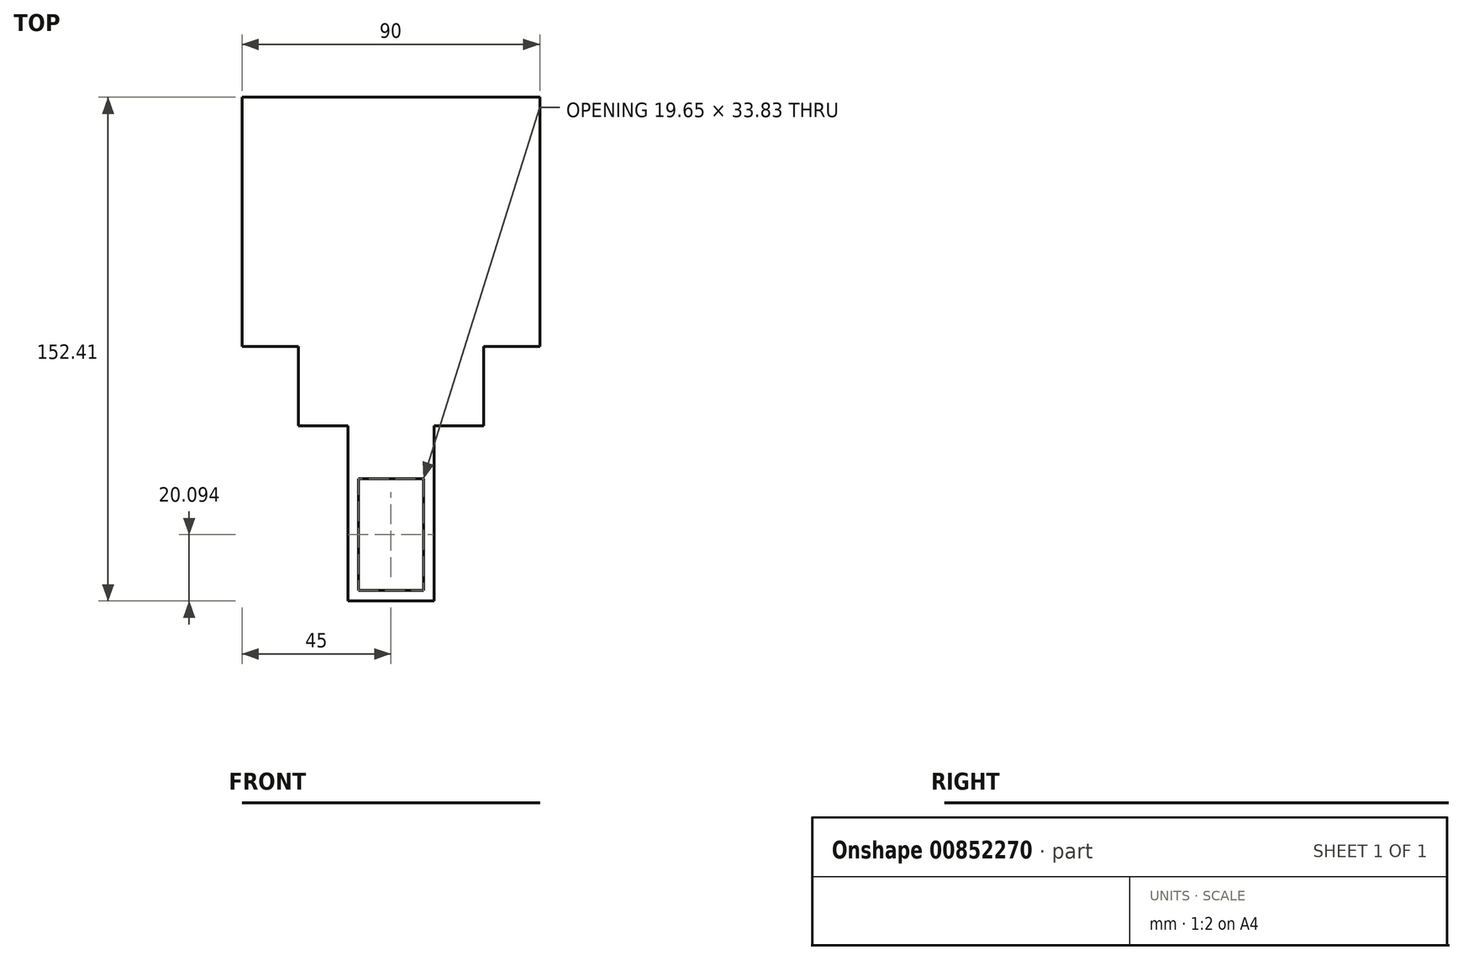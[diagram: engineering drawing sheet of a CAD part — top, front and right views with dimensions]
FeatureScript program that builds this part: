
annotation { "Feature Type Name" : "Feature", "Feature Type Description" : "" }
export const myFeature = defineFeature(function(context is Context, id is Id, definition is map)
    precondition{}
    {
        {
            var Q0;
            Q0=qCreatedBy(makeId("Top.planeOp"),FACE);
            var sketch = newSketch(context, id + "F0", { "sketchPlane" : qUnion([Q0])});
            skLineSegment(sketch, "E0.bottom", {"start": v(0, 0) * mm, "end": v(56, 0) * mm});
            skLineSegment(sketch, "E0.top", {"start": v(0, -74) * mm, "end": v(56, -74) * mm});
            skLineSegment(sketch, "E0.left", {"start": v(0, 0) * mm, "end": v(0, -74) * mm});
            skLineSegment(sketch, "E0.right", {"start": v(56, 0) * mm, "end": v(56, -74) * mm});
            skPoint(sketch, "E1", {"position": v(28, -74) * mm});
            skLineSegment(sketch, "E2", {"start": v(28, -74) * mm, "end": v(15, -74) * mm});
            skLineSegment(sketch, "E3", {"start": v(28, -74) * mm, "end": v(41, -74) * mm});
            skLineSegment(sketch, "E4", {"start": v(41, -74) * mm, "end": v(41, -90) * mm});
            skLineSegment(sketch, "E5", {"start": v(41, -90) * mm, "end": v(15, -90) * mm});
            skLineSegment(sketch, "E6", {"start": v(15, -74) * mm, "end": v(15, -90) * mm});
            skLineSegment(sketch, "E7", {"start": v(56, 0) * mm, "end": v(56, -23) * mm});
            skLineSegment(sketch, "E8", {"start": v(0, 0) * mm, "end": v(0, -23) * mm});
            skLineSegment(sketch, "E9", {"start": v(56, 0) * mm, "end": v(73, 0) * mm});
            skLineSegment(sketch, "E10", {"start": v(0, 0) * mm, "end": v(-17, 0) * mm});
            skPoint(sketch, "E11", {"position": v(28, 0) * mm});
            skPoint(sketch, "E12", {"position": v(28, -90) * mm});
            skLineSegment(sketch, "E13", {"start": v(28, -90) * mm, "end": v(41, -90) * mm});
            skLineSegment(sketch, "E14", {"start": v(73, 0) * mm, "end": v(73, -50) * mm});
            skLineSegment(sketch, "E15", {"start": v(-17, 0) * mm, "end": v(-17, -50) * mm});
            skLineSegment(sketch, "E16", {"start": v(-17, -50) * mm, "end": v(0, -50) * mm});
            skLineSegment(sketch, "E17", {"start": v(56, -50) * mm, "end": v(73, -50) * mm});
            skLineSegment(sketch, "E18", {"start": v(-17, 0) * mm, "end": v(-17, 25.4) * mm});
            skLineSegment(sketch, "E19", {"start": v(73, 0) * mm, "end": v(73, 25.4) * mm});
            skLineSegment(sketch, "E20", {"start": v(-17, 25.4) * mm, "end": v(73, 25.4) * mm});
            skLineSegment(sketch, "E21", {"start": v(15, -90) * mm, "end": v(15, -127) * mm});
            skLineSegment(sketch, "E22", {"start": v(41, -90) * mm, "end": v(41, -127) * mm});
            skLineSegment(sketch, "E23", {"start": v(15, -127) * mm, "end": v(41, -127) * mm});
            skLineSegment(sketch, "E24", {"start": v(41, -90) * mm, "end": v(37.83, -90) * mm});
            skLineSegment(sketch, "E25", {"start": v(37.83, -90) * mm, "end": v(37.83, -127) * mm});
            skLineSegment(sketch, "E26", {"start": v(15, -90) * mm, "end": v(18.18, -90) * mm});
            skLineSegment(sketch, "E27", {"start": v(18.18, -127) * mm, "end": v(18.18, -90) * mm});
            skLineSegment(sketch, "E28", {"start": v(73, 25.4) * mm, "end": v(69.83, 25.4) * mm});
            skLineSegment(sketch, "E29", {"start": v(69.83, 0) * mm, "end": v(69.83, 25.4) * mm});
            skLineSegment(sketch, "E30", {"start": v(-17, 0) * mm, "end": v(-13.83, 0) * mm});
            skLineSegment(sketch, "E31", {"start": v(-13.83, 25.4) * mm, "end": v(-13.83, 0) * mm});
            skLineSegment(sketch, "E32", {"start": v(15, -127) * mm, "end": v(15, -123.83) * mm});
            skLineSegment(sketch, "E33", {"start": v(15, -123.83) * mm, "end": v(41, -123.83) * mm});
            skLineSegment(sketch, "E34", {"start": v(37.83, -90) * mm, "end": v(34.65, -90) * mm});
            skLineSegment(sketch, "E35", {"start": v(18.18, -90) * mm, "end": v(21.35, -90) * mm});
            skLineSegment(sketch, "E36", {"start": v(21.35, -90) * mm, "end": v(21.35, -123.83) * mm});
            skLineSegment(sketch, "E37", {"start": v(21.35, -123.83) * mm, "end": v(34.65, -123.83) * mm});
            skLineSegment(sketch, "E38", {"start": v(34.65, -123.83) * mm, "end": v(34.65, -90) * mm});
            skSolve(sketch);
        }
        {
            var Q0;
            Q0=qSketchRegion(id+"F0",true);
            extrude(context, id + "F1", {"entities" : qUnion([Q0]), "depth" : 1 / 203.2 * mm, "offsetDistance" : 25.4 * mm});
        }
        {
            var Q0;
            {var subQ0=sQuery(id+"F0.wireOp",EDGE,"E36");Q0=makeQuery(id+"F0.imprint","IMPRINT",FACE,{"disambiguationData":[TD([[makeQuery(id+"F0.imprint","IMPRINT",EDGE,{"derivedFrom":subQ0}),1.0]])]});}
            extrude(context, id + "F2", {"entities" : qUnion([Q0]), "operationType" : NewBodyOperationType.REMOVE, "oppositeDirection" : true, "depth" : 25.4 * mm, "offsetDistance" : 25.4 * mm});
        }
    });
